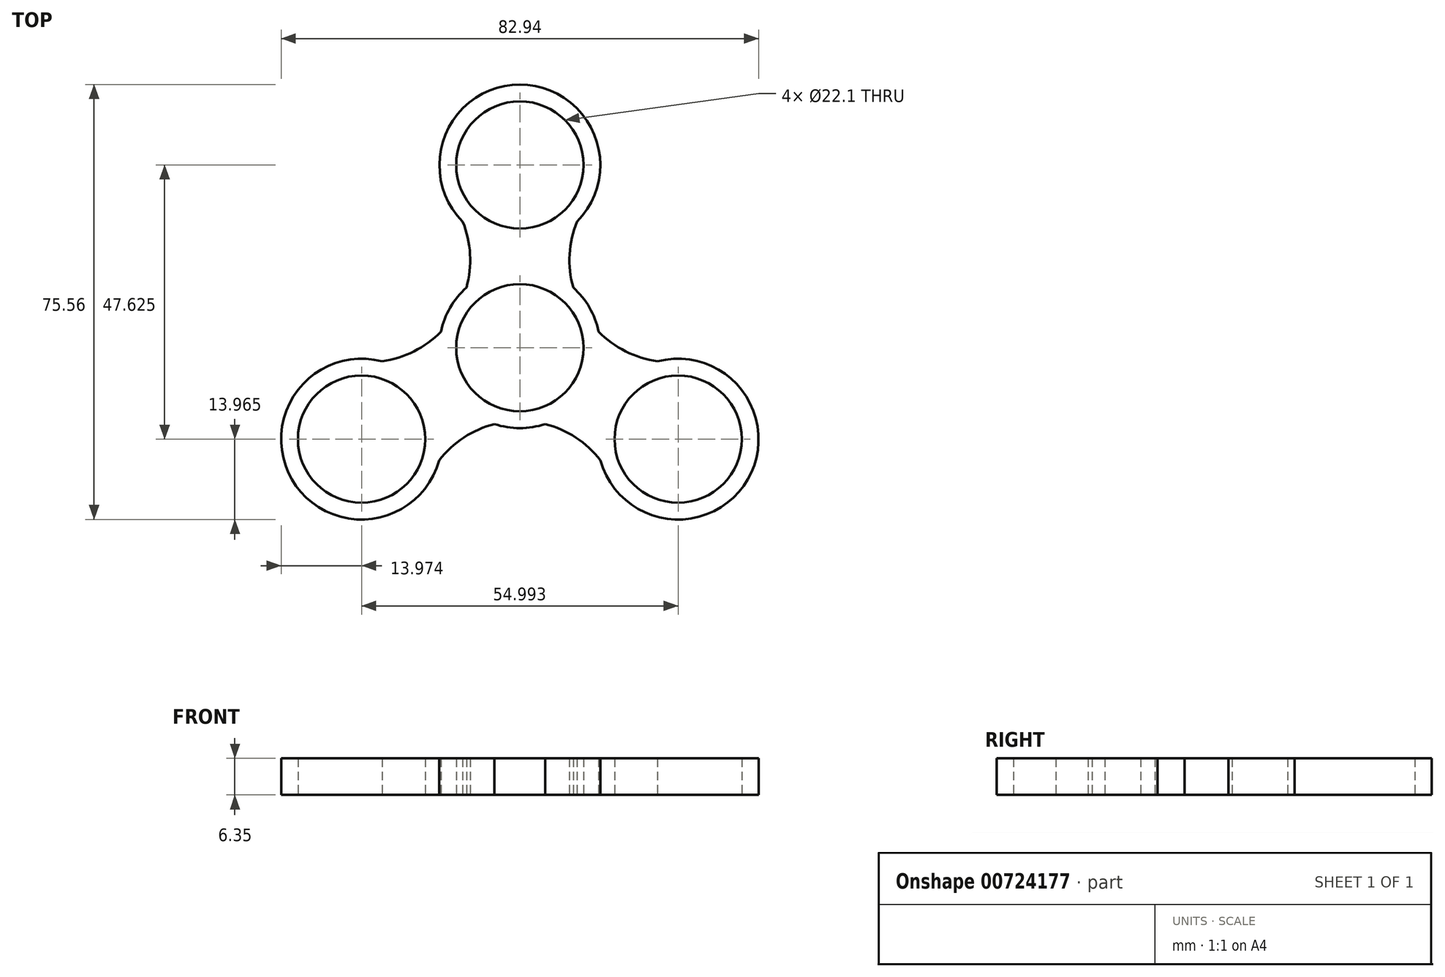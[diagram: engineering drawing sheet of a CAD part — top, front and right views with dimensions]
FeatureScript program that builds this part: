
annotation { "Feature Type Name" : "Feature", "Feature Type Description" : "" }
export const myFeature = defineFeature(function(context is Context, id is Id, definition is map)
    precondition{}
    {
        {
            var Q0;
            Q0=qCreatedBy(makeId("Top.planeOp"),FACE);
            var sketch = newSketch(context, id + "F0", { "sketchPlane" : qUnion([Q0])});
            skCircle(sketch, "E0", {"center": v(0, 0) * mm, "radius": 11.05 * mm});
            skCircle(sketch, "E1", {"center": v(0, 0) * mm, "radius": 13.97 * mm});
            skLineSegment(sketch, "E2", {"start": v(0, 0) * mm, "end": v(0, 31.75) * mm});
            skCircle(sketch, "E3", {"center": v(0, 31.75) * mm, "radius": 11.05 * mm});
            skCircle(sketch, "E4.1.0", {"center": v(-27.5, -15.87) * mm, "radius": 11.05 * mm});
            skCircle(sketch, "E4.2.0", {"center": v(27.5, -15.88) * mm, "radius": 11.05 * mm});
            skLineSegment(sketch, "E5", {"start": v(0, 0) * mm, "end": v(-26.4, 15.24) * mm});
            skCircle(sketch, "E6", {"center": v(0, 31.75) * mm, "radius": 13.97 * mm});
            skCircle(sketch, "E7.1.0", {"center": v(-27.5, -15.87) * mm, "radius": 13.97 * mm});
            skCircle(sketch, "E7.2.0", {"center": v(27.5, -15.88) * mm, "radius": 13.97 * mm});
            skArc(sketch, "E8", {"start": v(-30.1, -2.15) * mm, "mid": v(-11, 6.35) * mm, "end": v(-13.19, 27.14) * mm});
            skArc(sketch, "E9.1.0", {"start": v(16.91, -25) * mm, "mid": v(0, -12.7) * mm, "end": v(-16.91, -25) * mm});
            skArc(sketch, "E9.2.0", {"start": v(13.19, 27.14) * mm, "mid": v(11, 6.35) * mm, "end": v(30.1, -2.15) * mm});
            skSolve(sketch);
        }
        {
            var Q0;
            Q0 = qSketchRegion(id + "F0", true);
            extrude(context, id + "F1", {"entities" : qUnion([Q0]), "depth" : 6.35 * mm, "offsetDistance" : 25.4 * mm});
        }
    });
